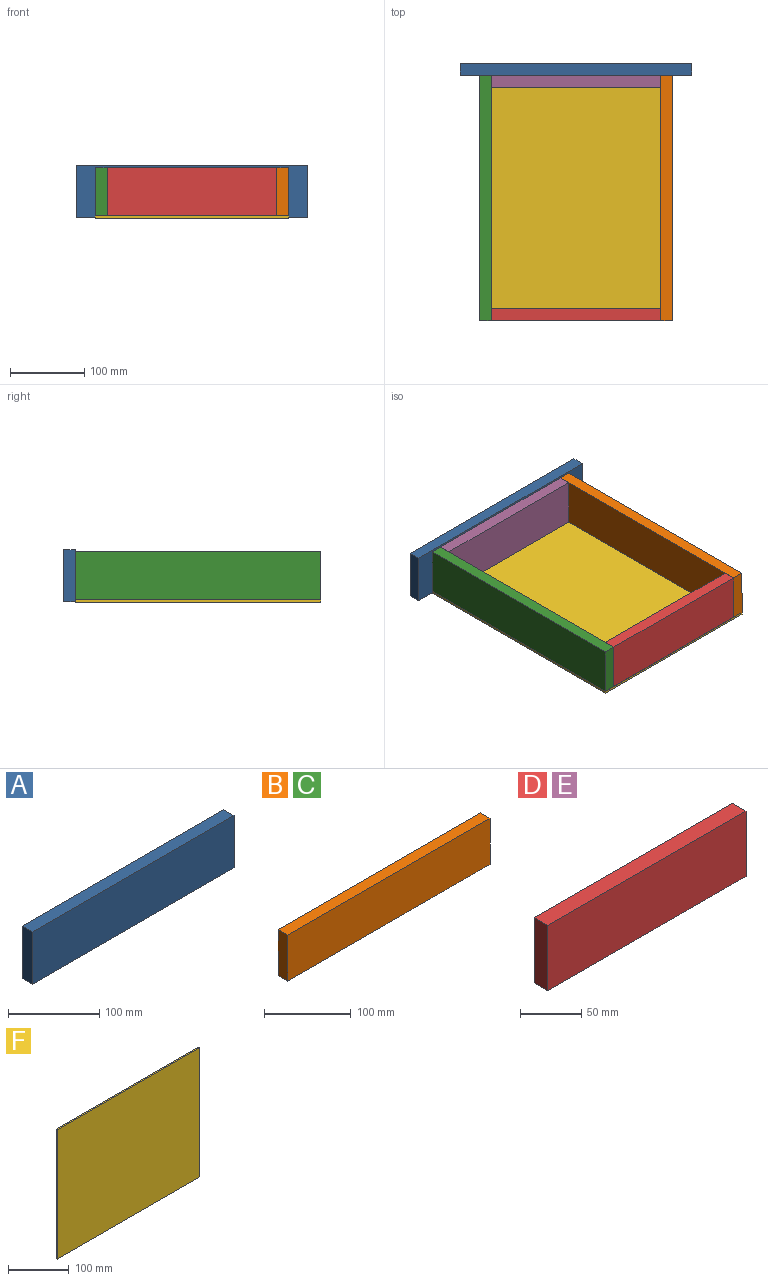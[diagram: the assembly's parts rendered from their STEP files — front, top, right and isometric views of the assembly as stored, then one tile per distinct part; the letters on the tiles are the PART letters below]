
ASSEMBLY  parts=6 mates=5
PART A: 6 faces, bbox 312x16x70 mm
  f0: plane 312x16mm, normal (0,0,1), area 4992mm2, adj f1,f3,f4,f5
  f1: plane 70x16mm, normal (-1,0,0), area 1120mm2, adj f0,f2,f4,f5
  f2: plane 312x16mm, normal (0,0,-1), area 4992mm2, adj f1,f3,f4,f5
  f3: plane 70x16mm, normal (1,0,0), area 1120mm2, adj f0,f2,f4,f5
  f4: plane 312x70mm, normal (0,-1,0), area 21840mm2, adj f0,f1,f2,f3
  f5: plane 312x70mm, normal (0,1,0), area 21840mm2, adj f0,f1,f2,f3
PART B: 6 faces, bbox 330x16x65 mm
  f0: plane 65x16mm, normal (-1,0,0), area 1040mm2, adj f1,f3,f4,f5
  f1: plane 330x16mm, normal (0,0,-1), area 5280mm2, adj f0,f2,f4,f5
  f2: plane 65x16mm, normal (1,0,0), area 1040mm2, adj f1,f3,f4,f5
  f3: plane 330x16mm, normal (0,0,1), area 5280mm2, adj f0,f2,f4,f5
  f4: plane 330x65mm, normal (0,-1,0), area 21450mm2, adj f0,f1,f2,f3
  f5: plane 330x65mm, normal (0,1,0), area 21450mm2, adj f0,f1,f2,f3
PART C: same geometry as B
PART D: 6 faces, bbox 228x16x65 mm
  f0: plane 228x16mm, normal (0,0,1), area 3648mm2, adj f1,f3,f4,f5
  f1: plane 65x16mm, normal (-1,0,0), area 1040mm2, adj f0,f2,f4,f5
  f2: plane 228x16mm, normal (0,0,-1), area 3648mm2, adj f1,f3,f4,f5
  f3: plane 65x16mm, normal (1,0,0), area 1040mm2, adj f0,f2,f4,f5
  f4: plane 228x65mm, normal (0,-1,0), area 14820mm2, adj f0,f1,f2,f3
  f5: plane 228x65mm, normal (0,1,0), area 14820mm2, adj f0,f1,f2,f3
PART E: same geometry as D
PART F: 6 faces, bbox 330x3x260 mm
  f0: plane 260x3mm, normal (-1,0,0), area 780mm2, adj f1,f3,f4,f5
  f1: plane 330x3mm, normal (0,0,-1), area 990mm2, adj f0,f2,f4,f5
  f2: plane 260x3mm, normal (1,0,0), area 780mm2, adj f1,f3,f4,f5
  f3: plane 330x3mm, normal (0,0,1), area 990mm2, adj f0,f2,f4,f5
  f4: plane 330x260mm, normal (0,-1,0), area 85800mm2, adj f0,f1,f2,f3
  f5: plane 330x260mm, normal (0,1,0), area 85800mm2, adj f0,f1,f2,f3
PLACE A rot(axis=(1,0,0),180deg) t=(-131.78,225.14,3.67)mm
PLACE B rot(axis=(0.71,0.71,0),180deg) t=(154.22,-104.86,71.17)mm
PLACE C rot(axis=(0.71,0.71,0),180deg) t=(-89.78,-104.86,71.17)mm
PLACE D t=(-89.78,-88.86,71.17)mm
PLACE E rot(axis=(1,0,0),180deg) t=(-89.78,209.14,6.17)mm
PLACE F rot(axis=(0.58,0.58,0.58),120deg) t=(-105.78,-104.86,6.17)mm
MATE fastened A.f5 <-> E.f4  axis (0,-1,0) through (24.22,225.14,38.67)mm
MATE fastened F.f5 <-> D.f2  axis (0,0,1) through (24.22,-104.86,6.17)mm
MATE fastened C.f5 <-> D.f1  axis (1,0,0) through (-89.78,-104.86,38.67)mm
MATE fastened C.f5 <-> E.f1  axis (1,0,0) through (-89.78,225.14,38.67)mm
MATE fastened E.f4 <-> B.f2  axis (0,1,0) through (138.22,225.14,38.67)mm
